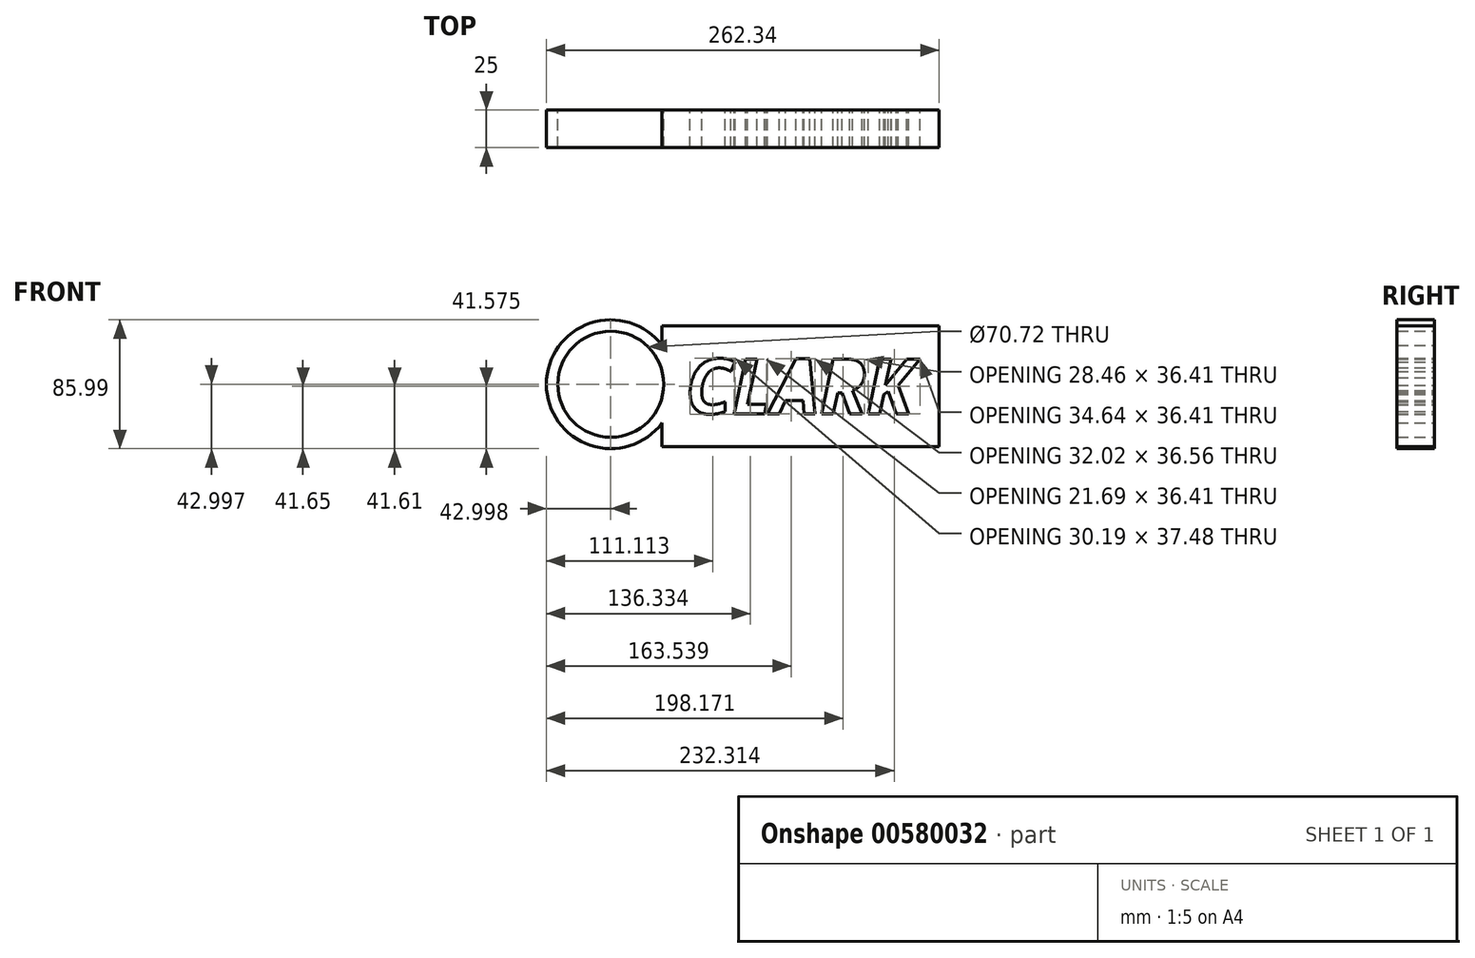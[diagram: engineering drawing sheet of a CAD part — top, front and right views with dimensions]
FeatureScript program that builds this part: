
annotation { "Feature Type Name" : "Feature", "Feature Type Description" : "" }
export const myFeature = defineFeature(function(context is Context, id is Id, definition is map)
    precondition{}
    {
        {
            var Q0;
            Q0=qCreatedBy(makeId("Front.planeOp"),FACE);
            var sketch = newSketch(context, id + "F0", { "sketchPlane" : qUnion([Q0])});
            skLineSegment(sketch, "E0.bottom", {"start": v(-123.06, 34.87) * mm, "end": v(61.94, 34.87) * mm});
            skLineSegment(sketch, "E0.top", {"start": v(-123.06, -45.83) * mm, "end": v(61.94, -45.83) * mm});
            skLineSegment(sketch, "E0.right", {"start": v(61.94, 34.87) * mm, "end": v(61.94, -45.83) * mm});
            skCircle(sketch, "E1", {"center": v(-157.4, -4.2) * mm, "radius": 43 * mm});
            skLineSegment(sketch, "E2", {"start": v(-123.06, -45.83) * mm, "end": v(-123.06, -30.07) * mm});
            skLineSegment(sketch, "E3", {"start": v(-123.06, 34.87) * mm, "end": v(-123.06, 21.68) * mm});
            skCircle(sketch, "E4", {"center": v(-157.4, -4.2) * mm, "radius": 35.36 * mm});
            skText(sketch, "E5", { "text": "CLARK", "fontName": "OpenSans-BoldItalic.ttf"});
            const initialGuessF0  = {"E5": [-0.10744, -0.02382, 1, 0, 0.03672]};
            skSetInitialGuess(sketch, initialGuessF0);
            skSolve(sketch);
        }
        {
            var Q0;
            Q0 = qSketchRegion(id + "F0", true);
            extrude(context, id + "F1", {"entities" : qUnion([Q0]), "depth" : 25 * mm, "offsetDistance" : 25 * mm});
        }
    });
